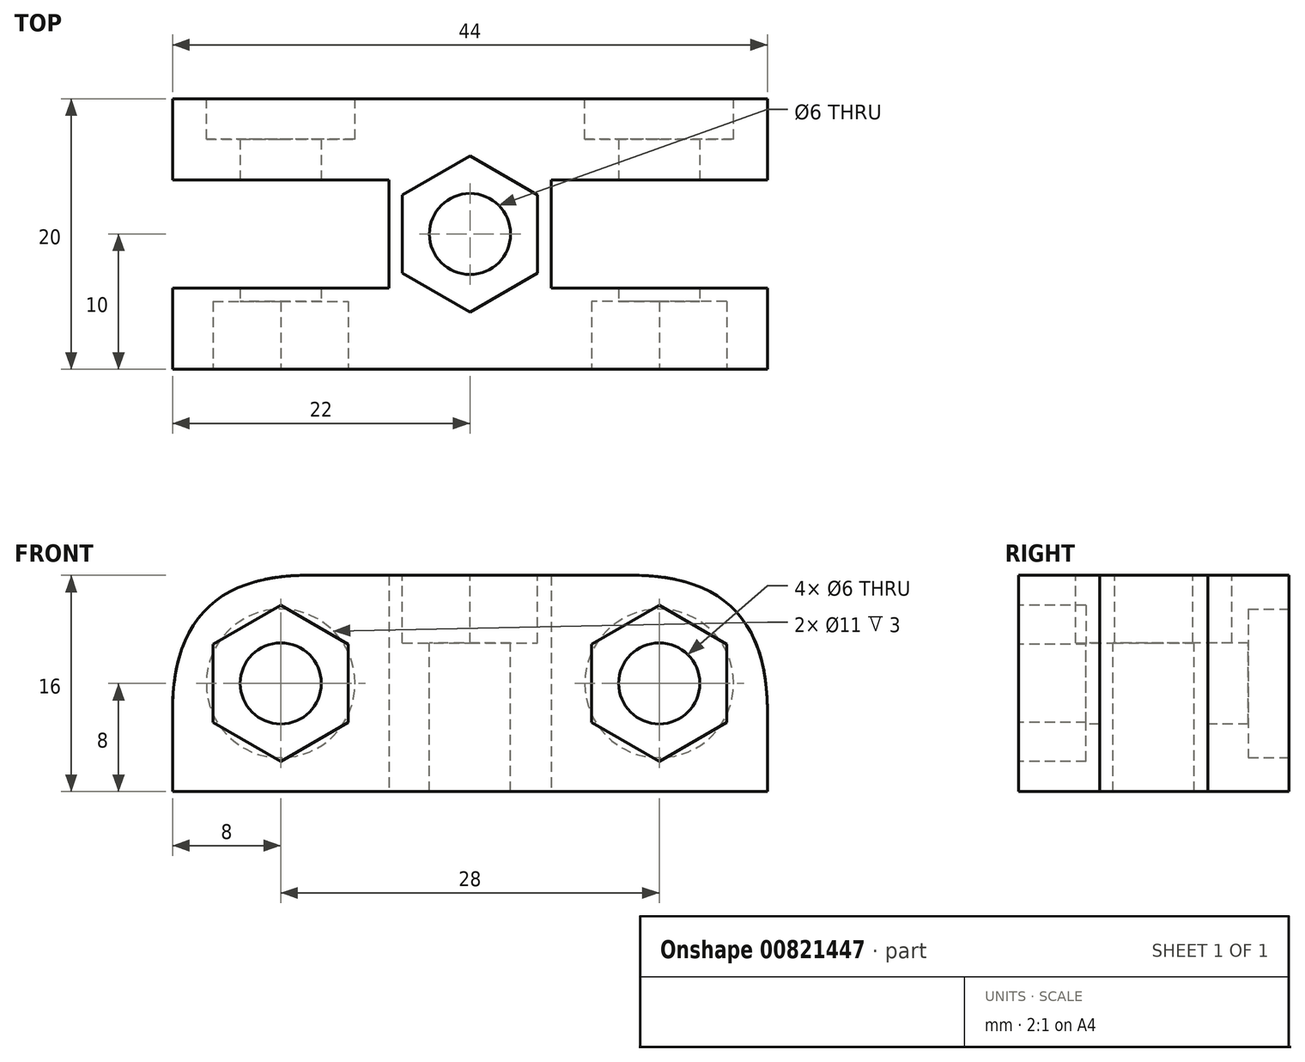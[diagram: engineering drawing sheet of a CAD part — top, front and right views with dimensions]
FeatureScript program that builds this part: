
annotation { "Feature Type Name" : "Feature", "Feature Type Description" : "" }
export const myFeature = defineFeature(function(context is Context, id is Id, definition is map)
    precondition{}
    {
        {
            var Q0;
            Q0=qCreatedBy(makeId("Top.planeOp"),FACE);
            var sketch = newSketch(context, id + "F0", { "sketchPlane" : qUnion([Q0])});
            skLineSegment(sketch, "E0.bottom", {"start": v(22, -10) * mm, "end": v(-22, -10) * mm});
            skLineSegment(sketch, "E0.top", {"start": v(22, 10) * mm, "end": v(-22, 10) * mm});
            skLineSegment(sketch, "E0.left", {"start": v(22, -10) * mm, "end": v(22, 10) * mm});
            skLineSegment(sketch, "E0.right", {"start": v(-22, -10) * mm, "end": v(-22, 10) * mm});
            skPoint(sketch, "E0.middle", {"position": v(0, 0) * mm});
            skSolve(sketch);
        }
        {
            var Q0;
            Q0 = qSketchRegion(id + "F0", true);
            extrude(context, id + "F1", {"entities" : qUnion([Q0]), "depth" : 16 * mm, "offsetDistance" : 25 * mm});
        }
        {
            var Q0;
            Q0=makeQuery(id+"F1.opExtrude","CAP_FACE",FACE,{"disambiguationData":[OSD([sQuery(id+"F0.wireOp",EDGE,"E0.bottom"),sQuery(id+"F0.wireOp",EDGE,"E0.top"),sQuery(id+"F0.wireOp",EDGE,"E0.left"),sQuery(id+"F0.wireOp",EDGE,"E0.right")])],"isStart":false});
            var sketch = newSketch(context, id + "F2", { "sketchPlane" : qUnion([Q0])});
            skCircle(sketch, "E1", {"center": v(0, 0) * mm, "radius": 3 * mm});
            skSolve(sketch);
        }
        {
            var Q0;
            Q0 = qSketchRegion(id + "F2", true);
            extrude(context, id + "F3", {"entities" : qUnion([Q0]), "operationType" : NewBodyOperationType.REMOVE, "endBound" : BoundingType.UP_TO_NEXT, "oppositeDirection" : true, "depth" : 25 * mm, "offsetDistance" : 25 * mm});
        }
        {
            var Q0;
            Q0=makeQuery(id+"F1.opExtrude","CAP_FACE",FACE,{"disambiguationData":[OSD([sQuery(id+"F0.wireOp",EDGE,"E0.bottom"),sQuery(id+"F0.wireOp",EDGE,"E0.top"),sQuery(id+"F0.wireOp",EDGE,"E0.left"),sQuery(id+"F0.wireOp",EDGE,"E0.right")])],"isStart":false});
            var sketch = newSketch(context, id + "F4", { "sketchPlane" : qUnion([Q0])});
            skCircle(sketch, "E2.cCircle", {"center": v(0, 0) * mm, "radius": 5 * mm, "construction": true});
            skLineSegment(sketch, "E2.0", {"start": v(5, 2.89) * mm, "end": v(5, -2.89) * mm});
            skLineSegment(sketch, "E2.1", {"start": v(5, -2.89) * mm, "end": v(0, -5.77) * mm});
            skLineSegment(sketch, "E2.2", {"start": v(0, -5.77) * mm, "end": v(-5, -2.89) * mm});
            skLineSegment(sketch, "E2.3", {"start": v(-5, -2.89) * mm, "end": v(-5, 2.89) * mm});
            skLineSegment(sketch, "E2.4", {"start": v(-5, 2.89) * mm, "end": v(0, 5.77) * mm});
            skLineSegment(sketch, "E2.5", {"start": v(0, 5.77) * mm, "end": v(5, 2.89) * mm});
            skPoint(sketch, "E2.0.midPoint", {"position": v(5, 0) * mm});
            skSolve(sketch);
        }
        {
            var Q0;
            Q0 = qSketchRegion(id + "F4", true);
            extrude(context, id + "F5", {"entities" : qUnion([Q0]), "operationType" : NewBodyOperationType.REMOVE, "oppositeDirection" : true, "depth" : 5 * mm, "offsetDistance" : 25 * mm});
        }
        {
            var Q0;
            Q0=makeQuery(id+"F1.opExtrude","CAP_EDGE",EDGE,{"disambiguationData":[OSD([sQuery(id+"F0.wireOp",EDGE,"E0.left")])],"isStart":false});
            var Q1;
            Q1=makeQuery(id+"F1.opExtrude","CAP_EDGE",EDGE,{"disambiguationData":[OSD([sQuery(id+"F0.wireOp",EDGE,"E0.right")])],"isStart":false});
            fillet(context, id + "F6", {"entities" : qUnion([Q0, Q1]), "radius" : 10 * mm, "tangentPropagation" : true, "rho" : 0.5, "crossSection" : FilletCrossSection.CONIC, "allowEdgeOverflow" : false});
        }
        {
            var Q0;
            Q0=makeQuery(id+"F1.opExtrude","SWEPT_FACE",FACE,{"disambiguationData":[OSD([sQuery(id+"F0.wireOp",EDGE,"E0.bottom")])]});
            var sketch = newSketch(context, id + "F7", { "sketchPlane" : qUnion([Q0])});
            skCircle(sketch, "E3", {"center": v(14, 8) * mm, "radius": 3 * mm});
            skCircle(sketch, "E4", {"center": v(-14, 8) * mm, "radius": 3 * mm});
            skSolve(sketch);
        }
        {
            var Q0;
            Q0 = qSketchRegion(id + "F7", true);
            extrude(context, id + "F8", {"entities" : qUnion([Q0]), "operationType" : NewBodyOperationType.REMOVE, "endBound" : BoundingType.UP_TO_NEXT, "oppositeDirection" : true, "depth" : 25 * mm, "offsetDistance" : 25 * mm});
        }
        {
            var Q0;
            Q0=makeQuery(id+"F1.opExtrude","SWEPT_FACE",FACE,{"disambiguationData":[OSD([sQuery(id+"F0.wireOp",EDGE,"E0.bottom")])]});
            var sketch = newSketch(context, id + "F9", { "sketchPlane" : qUnion([Q0])});
            skCircle(sketch, "E5.cCircle", {"center": v(14, 8) * mm, "radius": 5 * mm, "construction": true});
            skLineSegment(sketch, "E5.0", {"start": v(9, 5.11) * mm, "end": v(9, 10.89) * mm});
            skLineSegment(sketch, "E5.1", {"start": v(9, 10.89) * mm, "end": v(14, 13.77) * mm});
            skLineSegment(sketch, "E5.2", {"start": v(14, 13.77) * mm, "end": v(19, 10.89) * mm});
            skLineSegment(sketch, "E5.3", {"start": v(19, 10.89) * mm, "end": v(19, 5.11) * mm});
            skLineSegment(sketch, "E5.4", {"start": v(19, 5.11) * mm, "end": v(14, 2.23) * mm});
            skLineSegment(sketch, "E5.5", {"start": v(14, 2.23) * mm, "end": v(9, 5.11) * mm});
            skPoint(sketch, "E5.0.midPoint", {"position": v(9, 8) * mm});
            skCircle(sketch, "E6.cCircle", {"center": v(-14, 8) * mm, "radius": 5 * mm, "construction": true});
            skLineSegment(sketch, "E6.0", {"start": v(-9, 10.89) * mm, "end": v(-9, 5.11) * mm});
            skLineSegment(sketch, "E6.1", {"start": v(-9, 5.11) * mm, "end": v(-14, 2.23) * mm});
            skLineSegment(sketch, "E6.2", {"start": v(-14, 2.23) * mm, "end": v(-19, 5.11) * mm});
            skLineSegment(sketch, "E6.3", {"start": v(-19, 5.11) * mm, "end": v(-19, 10.89) * mm});
            skLineSegment(sketch, "E6.4", {"start": v(-19, 10.89) * mm, "end": v(-14, 13.77) * mm});
            skLineSegment(sketch, "E6.5", {"start": v(-14, 13.77) * mm, "end": v(-9, 10.89) * mm});
            skPoint(sketch, "E6.0.midPoint", {"position": v(-9, 8) * mm});
            skSolve(sketch);
        }
        {
            var Q0;
            Q0 = qSketchRegion(id + "F9", true);
            extrude(context, id + "F10", {"entities" : qUnion([Q0]), "operationType" : NewBodyOperationType.REMOVE, "oppositeDirection" : true, "depth" : 5 * mm, "offsetDistance" : 25 * mm});
        }
        {
            var Q0;
            Q0=makeQuery(id+"F1.opExtrude","SWEPT_FACE",FACE,{"disambiguationData":[OSD([sQuery(id+"F0.wireOp",EDGE,"E0.top")])]});
            var sketch = newSketch(context, id + "F11", { "sketchPlane" : qUnion([Q0])});
            skCircle(sketch, "E7", {"center": v(-14, 8) * mm, "radius": 5.5 * mm});
            skCircle(sketch, "E8", {"center": v(14, 8) * mm, "radius": 5.5 * mm});
            skSolve(sketch);
        }
        {
            var Q0;
            Q0 = qSketchRegion(id + "F11", true);
            extrude(context, id + "F12", {"entities" : qUnion([Q0]), "operationType" : NewBodyOperationType.REMOVE, "oppositeDirection" : true, "depth" : 3 * mm, "offsetDistance" : 25 * mm});
        }
        {
            var Q0;
            Q0=makeQuery(id+"F1.opExtrude","CAP_FACE",FACE,{"disambiguationData":[OSD([sQuery(id+"F0.wireOp",EDGE,"E0.bottom"),sQuery(id+"F0.wireOp",EDGE,"E0.top"),sQuery(id+"F0.wireOp",EDGE,"E0.left"),sQuery(id+"F0.wireOp",EDGE,"E0.right")])],"isStart":true});
            var sketch = newSketch(context, id + "F13", { "sketchPlane" : qUnion([Q0])});
            skLineSegment(sketch, "E9.bottom", {"start": v(-22, 4) * mm, "end": v(-6, 4) * mm});
            skLineSegment(sketch, "E9.top", {"start": v(-22, -4) * mm, "end": v(-6, -4) * mm});
            skLineSegment(sketch, "E9.left", {"start": v(-22, 4) * mm, "end": v(-22, -4) * mm});
            skLineSegment(sketch, "E9.right", {"start": v(-6, 4) * mm, "end": v(-6, -4) * mm});
            skLineSegment(sketch, "E10.bottom", {"start": v(22, 4) * mm, "end": v(6, 4) * mm});
            skLineSegment(sketch, "E10.top", {"start": v(22, -4) * mm, "end": v(6, -4) * mm});
            skLineSegment(sketch, "E10.left", {"start": v(22, 4) * mm, "end": v(22, -4) * mm});
            skLineSegment(sketch, "E10.right", {"start": v(6, 4) * mm, "end": v(6, -4) * mm});
            skSolve(sketch);
        }
        {
            var Q0;
            Q0 = qSketchRegion(id + "F13", true);
            extrude(context, id + "F14", {"entities" : qUnion([Q0]), "operationType" : NewBodyOperationType.REMOVE, "oppositeDirection" : true, "depth" : 25 * mm, "offsetDistance" : 25 * mm});
        }
    });
